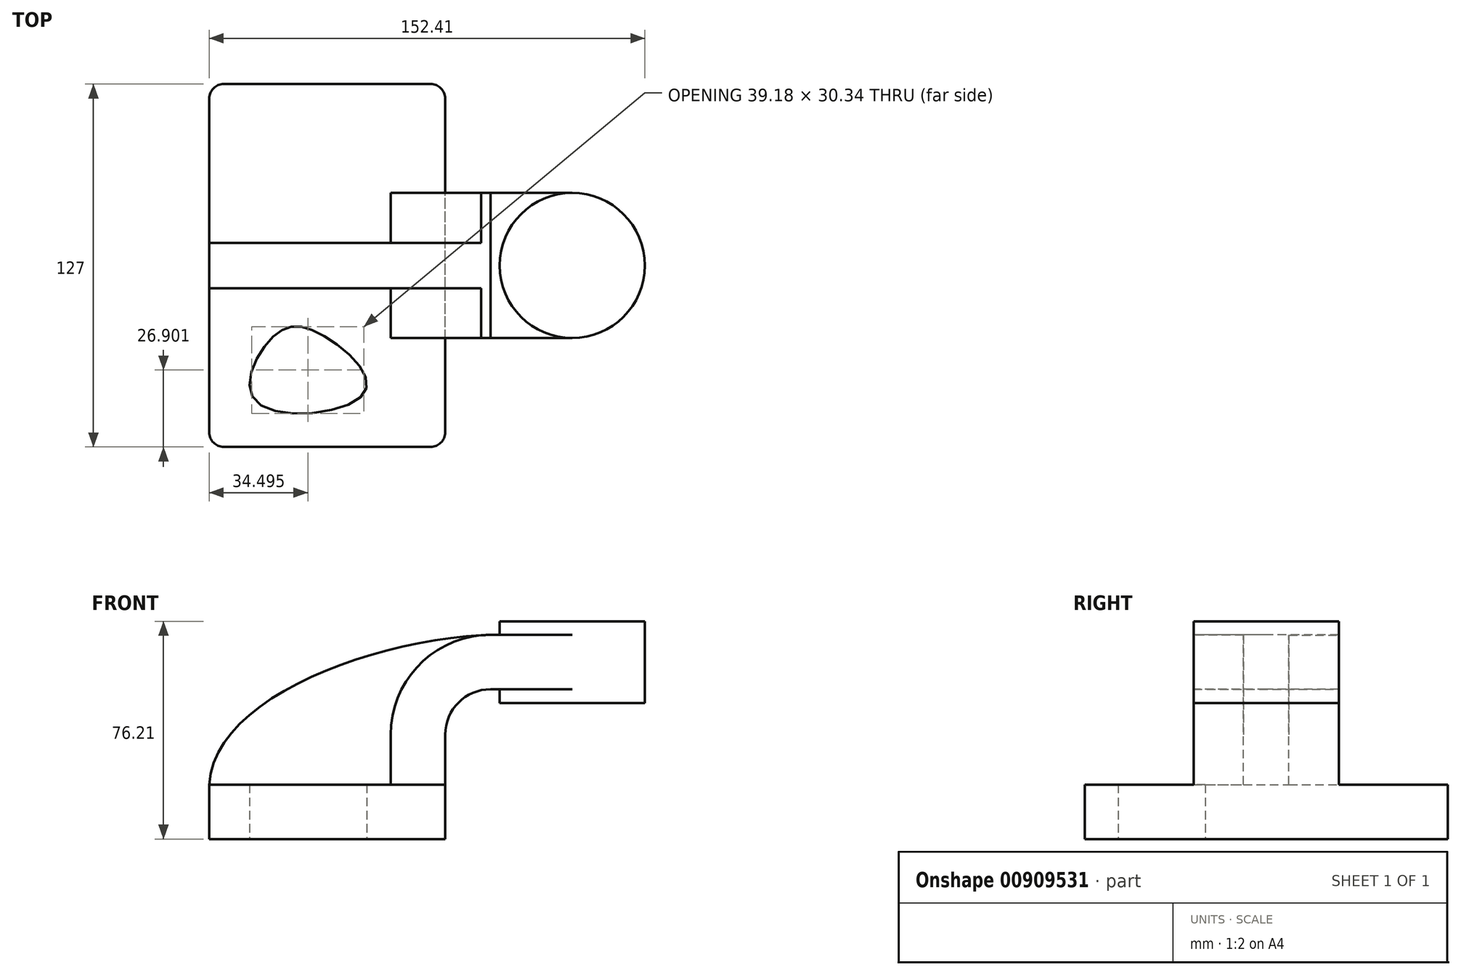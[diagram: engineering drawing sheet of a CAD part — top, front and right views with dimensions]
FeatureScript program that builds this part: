
annotation { "Feature Type Name" : "Feature", "Feature Type Description" : "" }
export const myFeature = defineFeature(function(context is Context, id is Id, definition is map)
    precondition{}
    {
        {
            var Q0;
            Q0=qCreatedBy(makeId("Front.planeOp"),FACE);
            var sketch = newSketch(context, id + "F0", { "sketchPlane" : qUnion([Q0])});
            skLineSegment(sketch, "E0.rect.bottom", {"start": v(-41.28, 9.52) * mm, "end": v(41.28, 9.52) * mm});
            skLineSegment(sketch, "E0.rect.top", {"start": v(-41.28, -9.52) * mm, "end": v(41.28, -9.52) * mm});
            skLineSegment(sketch, "E0.rect.left", {"start": v(-41.28, 9.52) * mm, "end": v(-41.28, -9.52) * mm});
            skLineSegment(sketch, "E0.rect.right", {"start": v(41.28, 9.52) * mm, "end": v(41.28, -9.52) * mm});
            skPoint(sketch, "E0.rect.middle", {"position": v(0, 0) * mm});
            skLineSegment(sketch, "E1", {"start": v(41.28, 9.52) * mm, "end": v(41.28, 27) * mm});
            skArc(sketch, "E2", {"start": v(41.28, 27) * mm, "mid": v(45.92, 38.23) * mm, "end": v(57.15, 42.88) * mm});
            skLineSegment(sketch, "E3", {"start": v(57.15, 42.88) * mm, "end": v(85.72, 42.88) * mm});
            skLineSegment(sketch, "E4.rect.bottom", {"start": v(60.32, 38.1) * mm, "end": v(111.12, 38.1) * mm});
            skLineSegment(sketch, "E4.rect.top", {"start": v(60.32, 66.68) * mm, "end": v(111.12, 66.68) * mm});
            skLineSegment(sketch, "E4.rect.left", {"start": v(60.32, 38.1) * mm, "end": v(60.32, 66.68) * mm});
            skLineSegment(sketch, "E4.rect.right", {"start": v(111.13, 38.1) * mm, "end": v(111.12, 66.68) * mm});
            skPoint(sketch, "E4.rect.middle", {"position": v(85.72, 52.39) * mm});
            skLineSegment(sketch, "E5.0", {"start": v(57.15, 61.93) * mm, "end": v(85.72, 61.93) * mm});
            skArc(sketch, "E5.1", {"start": v(22.23, 27) * mm, "mid": v(32.45, 51.7) * mm, "end": v(57.15, 61.93) * mm});
            skLineSegment(sketch, "E5.2", {"start": v(22.23, 9.52) * mm, "end": v(22.23, 27) * mm});
            skLineSegment(sketch, "E6", {"start": v(85.72, 38.1) * mm, "end": v(85.72, 66.68) * mm});
            skFitSpline(sketch, "E7", {"points": [v(-41.28, 9.53) * mm, v(57.15, 61.93) * mm], "startDerivative": vector(5.2, 92.34) * mm, "endDerivative": vector(120.92, 4.22) * mm});
            skSolve(sketch);
        }
        {
            var Q0;
            Q0=makeQuery(id+"F0.imprint","IMPRINT",FACE,{"disambiguationData":[TD([[makeQuery(id+"F0.imprint","IMPRINT",EDGE,{"derivedFrom":sQuery(id+"F0.wireOp",EDGE,"E0.rect.top")}),1.0]])]});
            extrude(context, id + "F1", {"entities" : qUnion([Q0]), "endBound" : BoundingType.SYMMETRIC, "depth" : 127 * mm});
        }
        {
            var Q0;
            {var subQ9=sQuery(id+"F0.wireOp",EDGE,"E1");Q0=makeQuery(id+"F0.imprint","IMPRINT",FACE,{"disambiguationData":[TD([[makeQuery(id+"F0.imprint","IMPRINT",EDGE,{"derivedFrom":subQ9}),1.0]])]});}
            var Q1;
            {var subQ0=sQuery(id+"F0.wireOp",EDGE,"E6");var subQ1=sQuery(id+"F0.wireOp",EDGE,"E3");var subQ2=makeQuery(id+"F0.imprint","INTERSECT",VERTEX,{"derivedFrom":[subQ1,subQ0]});Q1=makeQuery(id+"F0.imprint","IMPRINT",FACE,{"disambiguationData":[TD([[makeQuery(id+"F0.imprint","IMPRINT",EDGE,{"disambiguationData":[TD([[subQ2,1.0]])],"derivedFrom":subQ1}),1.0]])]});}
            extrude(context, id + "F2", {"entities" : qUnion([Q0, Q1]), "operationType" : NewBodyOperationType.ADD, "endBound" : BoundingType.SYMMETRIC, "depth" : 50.8 * mm});
        }
        {
            var Q0;
            {var subQ3=sQuery(id+"F0.wireOp",EDGE,"E5.2");Q0=makeQuery(id+"F0.imprint","IMPRINT",FACE,{"disambiguationData":[TD([[makeQuery(id+"F0.imprint","IMPRINT",EDGE,{"derivedFrom":subQ3}),1.0]])]});}
            extrude(context, id + "F3", {"entities" : qUnion([Q0]), "operationType" : NewBodyOperationType.ADD, "endBound" : BoundingType.SYMMETRIC, "depth" : 15.88 * mm});
        }
        {
            var Q0;
            {var subQ5=sQuery(id+"F0.wireOp",EDGE,"E4.rect.right");Q0=makeQuery(id+"F0.imprint","IMPRINT",FACE,{"disambiguationData":[TD([[makeQuery(id+"F0.imprint","IMPRINT",EDGE,{"derivedFrom":subQ5}),1.0]])]});}
            var Q1;
            Q1=sQuery(id+"F0.wireOp",EDGE,"E6");
            revolve(context, id + "F4", {"operationType" : NewBodyOperationType.ADD, "entities" : qUnion([Q0]), "axis" : qUnion([Q1]), "revolveType" : RevolveType.FULL});
        }
        {
            var Q0;
            Q0=makeQuery(id+"F1.opExtrude","CAP_EDGE",EDGE,{"disambiguationData":[OSD([sQuery(id+"F0.wireOp",EDGE,"E0.rect.right")])],"isStart":false});
            var Q1;
            Q1=makeQuery(id+"F1.opExtrude","CAP_EDGE",EDGE,{"disambiguationData":[OSD([sQuery(id+"F0.wireOp",EDGE,"E0.rect.left")])],"isStart":false});
            var Q2;
            Q2=makeQuery(id+"F1.opExtrude","CAP_EDGE",EDGE,{"disambiguationData":[OSD([sQuery(id+"F0.wireOp",EDGE,"E0.rect.right")])],"isStart":true});
            var Q3;
            Q3=makeQuery(id+"F1.opExtrude","CAP_EDGE",EDGE,{"disambiguationData":[OSD([sQuery(id+"F0.wireOp",EDGE,"E0.rect.left")])],"isStart":true});
            fillet(context, id + "F5", {"entities" : qUnion([Q0, Q1, Q2, Q3]), "radius" : 5.08 * mm, "tangentPropagation" : true, "allowEdgeOverflow" : false});
        }
        {
            var Q0;
            {var subQ4=sQuery(id+"F0.wireOp",EDGE,"E0.rect.bottom");var subQ5=sQuery(id+"F0.wireOp",EDGE,"E0.rect.right");var subQ6=sQuery(id+"F0.wireOp",EDGE,"E0.rect.left");Q0=makeQuery(id+"F3.boolean.opBoolean","SPLIT",FACE,{"disambiguationData":[TD([makeQuery(id+"F1.opExtrude","CAP_FACE",FACE,{"disambiguationData":[OSD([subQ4,sQuery(id+"F0.wireOp",EDGE,"E0.rect.top"),subQ6,subQ5])],"isStart":false})])],"derivedFrom":makeQuery(id+"F1.opExtrude","SWEPT_FACE",FACE,{"disambiguationData":[OSD([subQ4])]})});}
            var sketch = newSketch(context, id + "F6", { "sketchPlane" : qUnion([Q0])});
            skFitSpline(sketch, "E8", {"points": [v(-18.93, -24.9) * mm, v(-24.83, -47.66) * mm, v(13.17, -44.26) * mm, v(-2.88, -23.7) * mm, v(-18.93, -24.9) * mm]});
            skSolve(sketch);
        }
        {
            var Q0;
            Q0 = qSketchRegion(id + "F6", true);
            extrude(context, id + "F7", {"entities" : qUnion([Q0]), "operationType" : NewBodyOperationType.REMOVE, "endBound" : BoundingType.THROUGH_ALL, "oppositeDirection" : true, "depth" : 25.4 * mm, "offsetDistance" : 25.4 * mm});
        }
    });
